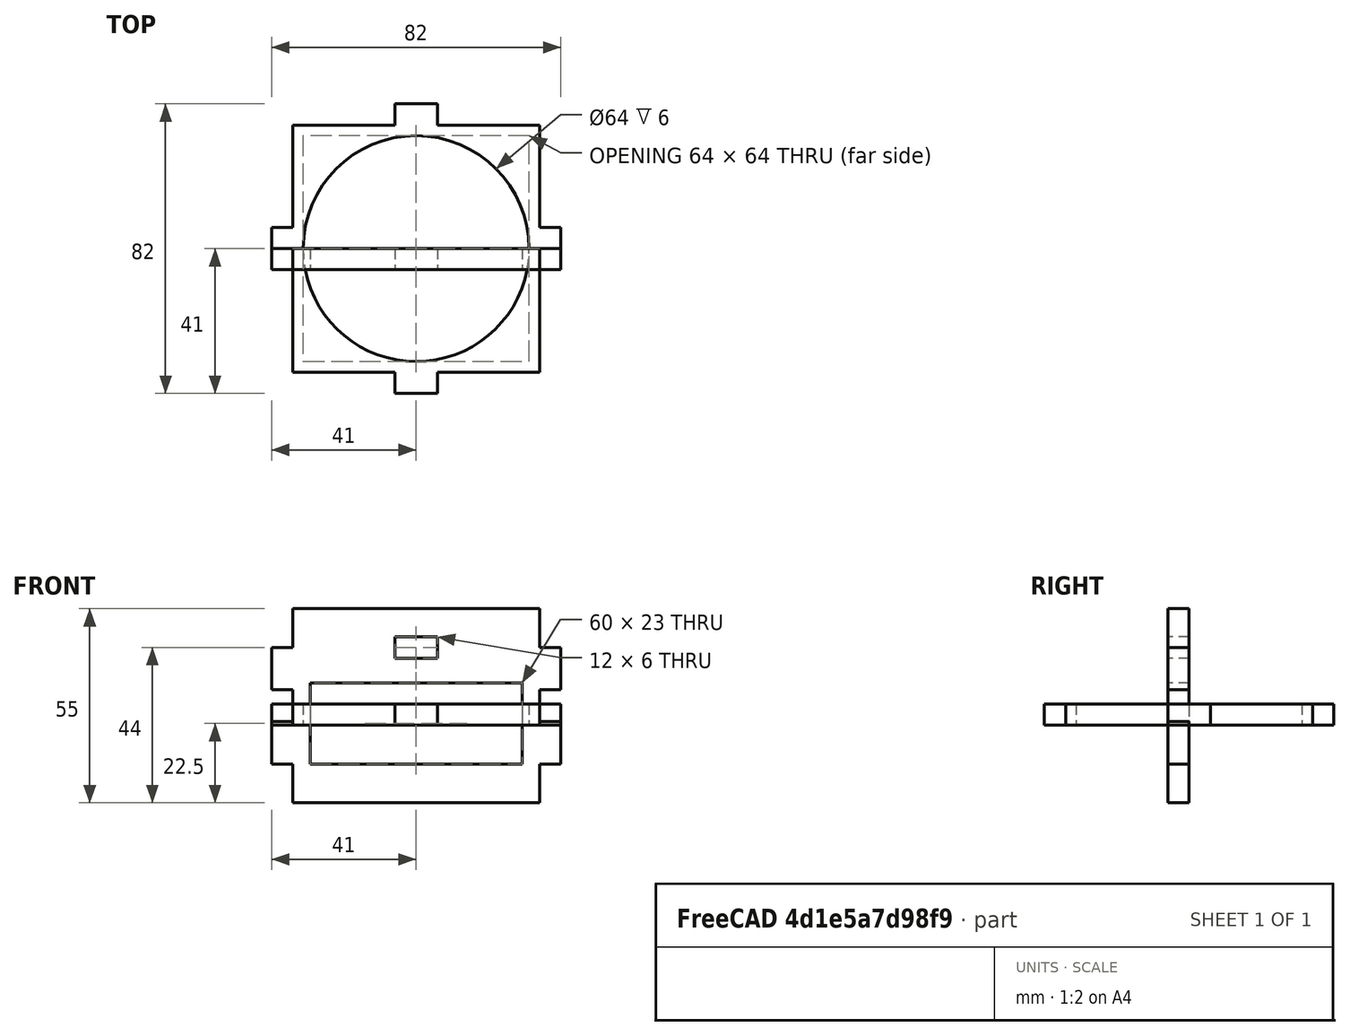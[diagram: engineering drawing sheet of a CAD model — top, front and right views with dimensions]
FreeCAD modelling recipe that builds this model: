
FCSTD DOCUMENT  (FreeCAD 1.0R39109 (Git))
Label: cupholder
License: All rights reserved
LicenseURL: https://en.wikipedia.org/wiki/All_rights_reserved
objects: App::Link×5, App::FeaturePython×5, PartDesign::Mirrored×4, Sketcher::SketchObject×3, PartDesign::Pad×3, PartDesign::Body×3, Part::Part2DObjectPython×3, App::VarSet×1, Assembly::JointGroup×1, Assembly::AssemblyObject×1
note: 29 computed .brp shape members not serialized (recipe doc carries the construction recipe); baked Part::Feature solids carry a one-line shape summary decoded from their .brp

FEATURE [App::VarSet] VarSet
  material = 6
FEATURE [Sketcher::SketchObject] Sketch
  ArcFitTolerance = 1e-06
  AttachmentSupport = -> [XZ_Plane]
  FullyConstrained = true
  MakeInternals = false
  MapMode = 5
  Placement = pos=(0,0,0) rot=(1,0,0;1.5708rad)
  expr: Constraints[24] = VarSet.material
  expr: Constraints[55] = VarSet.material
  sketch-geometry (20):
    g0: LineSegment StartX=0 StartY=33 StartZ=0 EndX=35 EndY=33 EndZ=0
    g1: LineSegment StartX=35 StartY=33 StartZ=0 EndX=35 EndY=22 EndZ=0
    g2: LineSegment StartX=35 StartY=22 StartZ=0 EndX=41 EndY=22 EndZ=0
    g3: LineSegment StartX=41 StartY=22 StartZ=0 EndX=41 EndY=10 EndZ=0
    g4: LineSegment StartX=41 StartY=10 StartZ=0 EndX=35 EndY=10 EndZ=0
    g5: LineSegment StartX=35 StartY=10 StartZ=0 EndX=35 EndY=1 EndZ=0
    g6: LineSegment StartX=35 StartY=1 StartZ=0 EndX=41 EndY=1 EndZ=0
    g7: LineSegment StartX=41 StartY=1 StartZ=0 EndX=41 EndY=-11 EndZ=0
    g8: LineSegment StartX=41 StartY=-11 StartZ=0 EndX=35 EndY=-11 EndZ=0
    g9: LineSegment StartX=35 StartY=-11 StartZ=0 EndX=35 EndY=-22 EndZ=0
    g10: LineSegment StartX=35 StartY=-22 StartZ=0 EndX=0 EndY=-22 EndZ=0
    g11: LineSegment StartX=0 StartY=33 StartZ=0 EndX=0 EndY=25 EndZ=0
    g12: LineSegment StartX=0 StartY=25 StartZ=0 EndX=6 EndY=25 EndZ=0
    g13: LineSegment StartX=6 StartY=25 StartZ=0 EndX=6 EndY=19 EndZ=0
    g14: LineSegment StartX=6 StartY=19 StartZ=0 EndX=0 EndY=19 EndZ=0
    g15: LineSegment StartX=0 StartY=19 StartZ=0 EndX=0 EndY=12 EndZ=0
    g16: LineSegment StartX=0 StartY=12 StartZ=0 EndX=30 EndY=12 EndZ=0
    g17: LineSegment StartX=30 StartY=12 StartZ=0 EndX=30 EndY=-11 EndZ=0
    g18: LineSegment StartX=30 StartY=-11 StartZ=0 EndX=0 EndY=-11 EndZ=0
    g19: LineSegment StartX=0 StartY=-11 StartZ=0 EndX=0 EndY=-22 EndZ=0
  constraints (60):
    c: PointOnObject(g0,g-2)
    c: Horizontal(g0)
    c: Coincident(g0,g1)
    c: Vertical(g1)
    c: Coincident(g1,g2)
    c: Horizontal(g2)
    c: Coincident(g2,g3)
    c: Vertical(g3)
    c: Coincident(g3,g4)
    c: Coincident(g4,g5)
    c: Vertical(g5)
    c: Coincident(g5,g6)
    c: Horizontal(g6)
    c: Coincident(g6,g7)
    c: Vertical(g7)
    c: Coincident(g7,g8)
    c: Coincident(g8,g9)
    c: Coincident(g9,g10)
    c: PointOnObject(g10,g-2)
    c: Horizontal(g10)
    c: Horizontal(g8)
    c: Horizontal(g4)
    c: Vertical(g9)
    c: Distance(g10,g0) = 55
    c: DistanceX(g2,g2) = 6
    c: Equal(g2,g4)
    c: Equal(g4,g6)
    c: Equal(g6,g8)
    c: DistanceY(g3,g3) = 12
    c: Equal(g3,g7)
    c: DistanceX(g0,g0) = 35
    c: DistanceY(g9,g9) = 11
    c: Distance(g10,g-1) = 22
    c: Equal(g1,g9)
    c: Coincident(g0,g11)
    c: Vertical(g11)
    c: Coincident(g11,g12)
    c: Horizontal(g12)
    c: Coincident(g12,g13)
    c: Vertical(g13)
    c: Coincident(g13,g14)
    c: PointOnObject(g14,g-2)
    c: Horizontal(g14)
    c: Coincident(g14,g15)
    c: PointOnObject(g15,g-2)
    c: Coincident(g15,g16)
    c: Horizontal(g16)
    c: Coincident(g16,g17)
    c: Vertical(g17)
    c: Coincident(g17,g18)
    c: PointOnObject(g18,g-2)
    c: Horizontal(g18)
    c: Coincident(g18,g19)
    c: Coincident(g19,g10)
    c: DistanceY(g11,g11) = 8
    c: DistanceY(g13,g13) = 6
    c: Distance(g19,g19) = 11
    c: DistanceX(g18,g18) = 30
    c: DistanceY(g15,g15) = 7
    c: DistanceX(g14,g14) = 6
FEATURE [PartDesign::Pad] Pad
  Direction = (0,-1,2e-16)
  Length = 6
  Length2 = 10
  Placement = pos=(0,0,0) rot=(1,0,0;1.5708rad)
  Profile = -> Sketch
  ReferenceAxis = -> Sketch [N_Axis]
  Refine = true
  Suppressed = false
  Type = 0
  expr: Length = VarSet.material
FEATURE [PartDesign::Mirrored] Mirrored
  BaseFeature = -> Pad
  MirrorPlane = -> Sketch [V_Axis]
  Originals = -> [Pad]
  Placement = pos=(0,0,0) rot=(1,0,0;1.5708rad)
  Refine = true
  Suppressed = false
  TransformMode = 0
FEATURE [PartDesign::Body] Body  label="out_part"
  AllowCompound = false
  Group = -> [Sketch,Pad,Mirrored]
  Origin = -> Origin
  Tip = -> Mirrored
FEATURE [Sketcher::SketchObject] Sketch001
  ArcFitTolerance = 1e-06
  AttachmentSupport = -> [XZ_Plane002]
  FullyConstrained = true
  MakeInternals = false
  MapMode = 5
  Placement = pos=(0,0,0) rot=(1,0,0;1.5708rad)
  expr: Constraints[22] = 35 mm + VarSet.material
  expr: Constraints[26] = VarSet.material
  expr: Constraints[52] = VarSet.material
  sketch-geometry (20):
    g0: LineSegment StartX=0 StartY=33 StartZ=0 EndX=41 EndY=33 EndZ=0
    g1: LineSegment StartX=41 StartY=33 StartZ=0 EndX=41 EndY=22 EndZ=0
    g2: LineSegment StartX=41 StartY=22 StartZ=0 EndX=35 EndY=22 EndZ=0
    g3: LineSegment StartX=35 StartY=22 StartZ=0 EndX=35 EndY=10 EndZ=0
    g4: LineSegment StartX=35 StartY=10 StartZ=0 EndX=41 EndY=10 EndZ=0
    g5: LineSegment StartX=41 StartY=10 StartZ=0 EndX=41 EndY=1 EndZ=0
    g6: LineSegment StartX=41 StartY=1 StartZ=0 EndX=35 EndY=1 EndZ=0
    g7: LineSegment StartX=35 StartY=1 StartZ=0 EndX=35 EndY=-11 EndZ=0
    g8: LineSegment StartX=35 StartY=-11 StartZ=0 EndX=41 EndY=-11 EndZ=0
    g9: LineSegment StartX=41 StartY=-11 StartZ=0 EndX=41 EndY=-22 EndZ=0
    g10: LineSegment StartX=41 StartY=-22 StartZ=0 EndX=0 EndY=-22 EndZ=0
    g11: LineSegment StartX=0 StartY=33 StartZ=0 EndX=0 EndY=25 EndZ=0
    g12: LineSegment StartX=0 StartY=25 StartZ=0 EndX=6 EndY=25 EndZ=0
    g13: LineSegment StartX=6 StartY=25 StartZ=0 EndX=6 EndY=19 EndZ=0
    g14: LineSegment StartX=6 StartY=19 StartZ=0 EndX=0 EndY=19 EndZ=0
    g15: LineSegment StartX=0 StartY=19 StartZ=0 EndX=0 EndY=12 EndZ=0
    g16: LineSegment StartX=0 StartY=12 StartZ=0 EndX=30 EndY=12 EndZ=0
    g17: LineSegment StartX=30 StartY=12 StartZ=0 EndX=30 EndY=-11 EndZ=0
    g18: LineSegment StartX=30 StartY=-11 StartZ=0 EndX=0 EndY=-11 EndZ=0
    g19: LineSegment StartX=0 StartY=-11 StartZ=0 EndX=0 EndY=-22 EndZ=0
  constraints (60):
    c: PointOnObject(g0,g-2)
    c: Horizontal(g0)
    c: Coincident(g0,g1)
    c: Vertical(g1)
    c: Coincident(g1,g2)
    c: Horizontal(g2)
    c: Coincident(g2,g3)
    c: Vertical(g3)
    c: Coincident(g3,g4)
    c: Horizontal(g4)
    c: Coincident(g4,g5)
    c: Vertical(g5)
    c: Coincident(g5,g6)
    c: Horizontal(g6)
    c: Coincident(g6,g7)
    c: Vertical(g7)
    c: Coincident(g7,g8)
    c: Horizontal(g8)
    c: Coincident(g8,g9)
    c: Vertical(g9)
    c: Coincident(g9,g10)
    c: PointOnObject(g10,g-2)
    c: DistanceX(g0,g0) = 41
    c: Equal(g0,g10)
    c: Horizontal(g10)
    c: DistanceY(g3,g3) = 12
    c: DistanceX(g4,g4) = 6
    c: Equal(g2,g4)
    c: Equal(g4,g6)
    c: Equal(g3,g7)
    c: Distance(g10,g0) = 55
    c: DistanceY(g9,g9) = 11
    c: Distance(g-1,g10) = 22
    c: Equal(g1,g9)
    c: Coincident(g0,g11)
    c: PointOnObject(g11,g-2)
    c: Coincident(g11,g12)
    c: Horizontal(g12)
    c: Coincident(g12,g13)
    c: Coincident(g13,g14)
    c: PointOnObject(g14,g-2)
    c: Horizontal(g14)
    c: Coincident(g14,g15)
    c: PointOnObject(g15,g-2)
    c: Coincident(g15,g16)
    c: Horizontal(g16)
    c: Coincident(g16,g17)
    c: Vertical(g17)
    c: Coincident(g17,g18)
    c: PointOnObject(g18,g-2)
    c: Coincident(g18,g19)
    c: Coincident(g19,g10)
    c: DistanceY(g13,g13) = 6
    c: DistanceY(g11,g11) = 8
    c: DistanceX(g12,g12) = 6
    c: Vertical(g13)
    c: DistanceY(g15,g15) = 7
    c: DistanceY(g19,g19) = 11
    c: Horizontal(g18)
    c: DistanceX(g18,g18) = 30
FEATURE [PartDesign::Pad] Pad001
  Direction = (0,-1,2e-16)
  Length = 6
  Length2 = 10
  Placement = pos=(0,0,0) rot=(1,0,0;1.5708rad)
  Profile = -> Sketch001
  ReferenceAxis = -> Sketch001 [N_Axis]
  Refine = true
  Suppressed = false
  Type = 0
  expr: Length = VarSet.material
FEATURE [PartDesign::Mirrored] Mirrored001
  BaseFeature = -> Pad001
  MirrorPlane = -> Sketch001 [V_Axis]
  Originals = -> [Pad001]
  Placement = pos=(0,0,0) rot=(1,0,0;1.5708rad)
  Refine = true
  Suppressed = false
  TransformMode = 0
FEATURE [PartDesign::Body] Body002  label="in_part"
  AllowCompound = false
  Group = -> [Sketch001,Pad001,Mirrored001]
  Origin = -> Origin002
  Tip = -> Mirrored001
FEATURE [App::Link] out_part  label="out_part001"
  LinkedObject = -> Body
FEATURE [App::FeaturePython] GroundedJoint  # Assembly grounded joint (typed FeaturePython)
  ObjectToGround = -> out_part
FEATURE [App::Link] out_part001  label="out_part002"
  LinkPlacement = pos=(-1.6e-14,76,-2.3e-15) rot=(0,0,1;0rad)
  LinkedObject = -> Body
  Placement = pos=(-1.6e-14,76,-2.3e-15) rot=(0,0,1;0rad)
FEATURE [App::Link] in_part  label="in_part001"
  LinkPlacement = pos=(-41,35,4.09813e-11) rot=(0,0,1;1.5708rad)
  LinkedObject = -> Body002
  Placement = pos=(-41,35,4.09813e-11) rot=(0,0,1;1.5708rad)
FEATURE [App::Link] in_part001  label="in_part002"
  LinkPlacement = pos=(41,35,1.12506e-11) rot=(0,0,-1;1.5708rad)
  LinkedObject = -> Body002
  Placement = pos=(41,35,1.12506e-11) rot=(0,0,-1;1.5708rad)
FEATURE [App::FeaturePython] Joint  label="Fixed"  # Assembly joint (typed FeaturePython)
  Activated = true
  AngleMax = 0
  AngleMin = 0
  Detach1 = false
  Detach2 = false
  Distance = 0
  Distance2 = 0
  EnableAngleMax = false
  EnableAngleMin = false
  EnableLengthMax = false
  EnableLengthMin = false
  JointType = 0 (Fixed)
  LengthMax = 0
  LengthMin = 0
  Offset2 = pos=(0,0,0) rot=(0,0,-1;1.5708rad)
  Placement1 = pos=(-41,-6,5.5) rot=(0,1,0;3.14159rad)
  Placement2 = pos=(-35,-6,5.5) rot=(-0.707107,0.707107,0;3.14159rad)
  Reference1 = -> Assembly [in_part.Edge46,in_part.Edge46]
  Reference2 = -> Assembly [out_part.Edge46,out_part.Edge46]
FEATURE [App::FeaturePython] Joint001  label="Fixed001"  # Assembly joint (typed FeaturePython)
  Activated = true
  AngleMax = 0
  AngleMin = 0
  Detach1 = false
  Detach2 = false
  Distance = 0
  Distance2 = 0
  EnableAngleMax = false
  EnableAngleMin = false
  EnableLengthMax = false
  EnableLengthMin = false
  JointType = 0 (Fixed)
  LengthMax = 0
  LengthMin = 0
  Offset2 = pos=(0,0,0) rot=(0,0,1;1.5708rad)
  Placement1 = pos=(35,7.1e-15,16) rot=(0,1,0;3.14159rad)
  Placement2 = pos=(41,3.6e-15,16) rot=(0.707107,0.707107,0;3.14159rad)
  Reference1 = -> Assembly [in_part001.Edge9,in_part001.Edge9]
  Reference2 = -> Assembly [out_part.Edge9,out_part.Edge9]
FEATURE [App::FeaturePython] Joint002  label="Fixed002"  # Assembly joint (typed FeaturePython)
  Activated = true
  AngleMax = 0
  AngleMin = 0
  Detach1 = false
  Detach2 = false
  Distance = 0
  Distance2 = 0
  EnableAngleMax = false
  EnableAngleMin = false
  EnableLengthMax = false
  EnableLengthMin = false
  JointType = 0 (Fixed)
  LengthMax = 0
  LengthMin = 0
  Offset2 = pos=(0,0,0) rot=(0,0,-1;1.5708rad)
  Placement1 = pos=(41,-6,16) rot=(0,1,0;3.14159rad)
  Placement2 = pos=(-35,7.1e-15,16) rot=(-0.707107,0.707107,0;3.14159rad)
  Reference1 = -> Assembly [out_part001.Edge10,out_part001.Edge10]
  Reference2 = -> Assembly [in_part001.Edge39,in_part001.Edge39]
FEATURE [Sketcher::SketchObject] Sketch002
  ArcFitTolerance = 1e-06
  AttachmentSupport = -> [XY_Plane004]
  FullyConstrained = true
  MakeInternals = false
  MapMode = 5
  expr: Constraints[21] = VarSet.material
  sketch-geometry (9):
    g0: ArcOfCircle CenterX=0 CenterY=0 CenterZ=0 NormalX=0 NormalY=0 NormalZ=1 AngleXU=0 Radius=32 StartAngle=0 EndAngle=1.5708
    g1: LineSegment StartX=0 StartY=32 StartZ=0 EndX=0 EndY=41 EndZ=0
    g2: LineSegment StartX=0 StartY=41 StartZ=0 EndX=6 EndY=41 EndZ=0
    g3: LineSegment StartX=6 StartY=41 StartZ=0 EndX=6 EndY=35 EndZ=0
    g4: LineSegment StartX=6 StartY=35 StartZ=0 EndX=35 EndY=35 EndZ=0
    g5: LineSegment StartX=35 StartY=35 StartZ=0 EndX=35 EndY=6 EndZ=0
    g6: LineSegment StartX=35 StartY=6 StartZ=0 EndX=41 EndY=6 EndZ=0
    g7: LineSegment StartX=41 StartY=6 StartZ=0 EndX=41 EndY=0 EndZ=0
    g8: LineSegment StartX=41 StartY=0 StartZ=0 EndX=32 EndY=0 EndZ=0
  constraints (27):
    c: Coincident(g0,g-1)
    c: PointOnObject(g0,g-2)
    c: PointOnObject(g0,g-1)
    c: Coincident(g0,g1)
    c: PointOnObject(g1,g-2)
    c: Coincident(g1,g2)
    c: Horizontal(g2)
    c: Coincident(g2,g3)
    c: Vertical(g3)
    c: Coincident(g3,g4)
    c: Horizontal(g4)
    c: Coincident(g4,g5)
    c: Vertical(g5)
    c: Coincident(g5,g6)
    c: Horizontal(g6)
    c: Coincident(g6,g7)
    c: PointOnObject(g7,g-1)
    c: Vertical(g7)
    c: Coincident(g7,g8)
    c: Coincident(g8,g0)
    c: DistanceX(g2,g2) = 6
    c: DistanceY(g3,g3) = 6
    c: Equal(g1,g8)
    c: Equal(g2,g7)
    c: Radius(g0) = 32
    c: Distance(g1,g5) = 35
    c: Distance(g-1,g4) = 35
FEATURE [PartDesign::Pad] Pad002
  Direction = (0,0,1)
  Length = 6
  Length2 = 10
  Profile = -> Sketch002
  ReferenceAxis = -> Sketch002 [N_Axis]
  Refine = true
  Suppressed = false
  Type = 0
  expr: Length = VarSet.material
FEATURE [PartDesign::Mirrored] Mirrored002
  BaseFeature = -> Pad002
  MirrorPlane = -> Sketch002 [V_Axis]
  Originals = -> [Pad002]
  Refine = true
  Suppressed = false
  TransformMode = 0
FEATURE [PartDesign::Mirrored] Mirrored003
  BaseFeature = -> Mirrored002
  MirrorPlane = -> XZ_Plane004
  Originals = -> [Mirrored002]
  Refine = true
  Suppressed = false
  TransformMode = 1
FEATURE [PartDesign::Body] Body003  label="cup_place"
  AllowCompound = false
  Group = -> [Sketch002,Pad002,Mirrored002,Mirrored003]
  Origin = -> Origin004
  Tip = -> Mirrored003
FEATURE [App::Link] cup_place  label="cup_place001"
  LinkPlacement = pos=(-1.71e-14,35,19) rot=(0,0,1;0rad)
  LinkedObject = -> Body003
  Placement = pos=(-1.71e-14,35,19) rot=(0,0,1;0rad)
FEATURE [App::FeaturePython] Joint003  label="Fixed003"  # Assembly joint (typed FeaturePython)
  Activated = true
  AngleMax = 0
  AngleMin = 0
  Detach1 = false
  Detach2 = false
  Distance = 0
  Distance2 = 0
  EnableAngleMax = false
  EnableAngleMin = false
  EnableLengthMax = false
  EnableLengthMin = false
  JointType = 0 (Fixed)
  LengthMax = 0
  LengthMin = 0
  Offset2 = pos=(0,0,0) rot=(0,0,1;3.14159rad)
  Placement1 = pos=(41,0,0) rot=(-0.57735,-0.57735,0.57735;4.18879rad)
  Placement2 = pos=(0,0,19) rot=(0,-1,0;4.71239rad)
  Reference1 = -> Assembly [cup_place.Edge29,cup_place.Edge29]
  Reference2 = -> Assembly [in_part001.Edge67,in_part001.Edge67]
FEATURE [Assembly::JointGroup] Joints
  Group = -> [GroundedJoint,Joint,Joint001,Joint002,Joint003]
FEATURE [Assembly::AssemblyObject] Assembly
  Group = -> [Joints,out_part,GroundedJoint,out_part001,in_part,in_part001,Joint,Joint001,Joint002,cup_place,Joint003]
  Origin = -> Origin003
  Type = Assembly
FEATURE [Part::Part2DObjectPython] Shape2DView  # Draft 2D object (typed FeaturePython)
  AutoUpdate = true
  Base = -> Mirrored
  Clip = false
  FaceNumbers = [19]
  FuseArch = false
  HiddenLines = false
  InPlace = true
  OnlySolids = false
  Projection = (0,1,0)
  ProjectionMode = 0
  SegmentLength = 0.05
  Tessellation = false
  VisibleOnly = false
FEATURE [Part::Part2DObjectPython] Shape2DView001  # Draft 2D object (typed FeaturePython)
  AutoUpdate = true
  Base = -> Mirrored001
  Clip = false
  FaceNumbers = [19]
  FuseArch = false
  HiddenLines = false
  InPlace = true
  OnlySolids = false
  Projection = (0,1,0)
  ProjectionMode = 0
  SegmentLength = 0.05
  Tessellation = false
  VisibleOnly = false
FEATURE [Part::Part2DObjectPython] Shape2DView002  # Draft 2D object (typed FeaturePython)
  AutoUpdate = true
  Base = -> Mirrored003
  Clip = false
  FaceNumbers = [19]
  FuseArch = false
  HiddenLines = false
  InPlace = true
  OnlySolids = false
  Projection = (0,0,1)
  ProjectionMode = 0
  SegmentLength = 0.05
  Tessellation = false
  VisibleOnly = false
